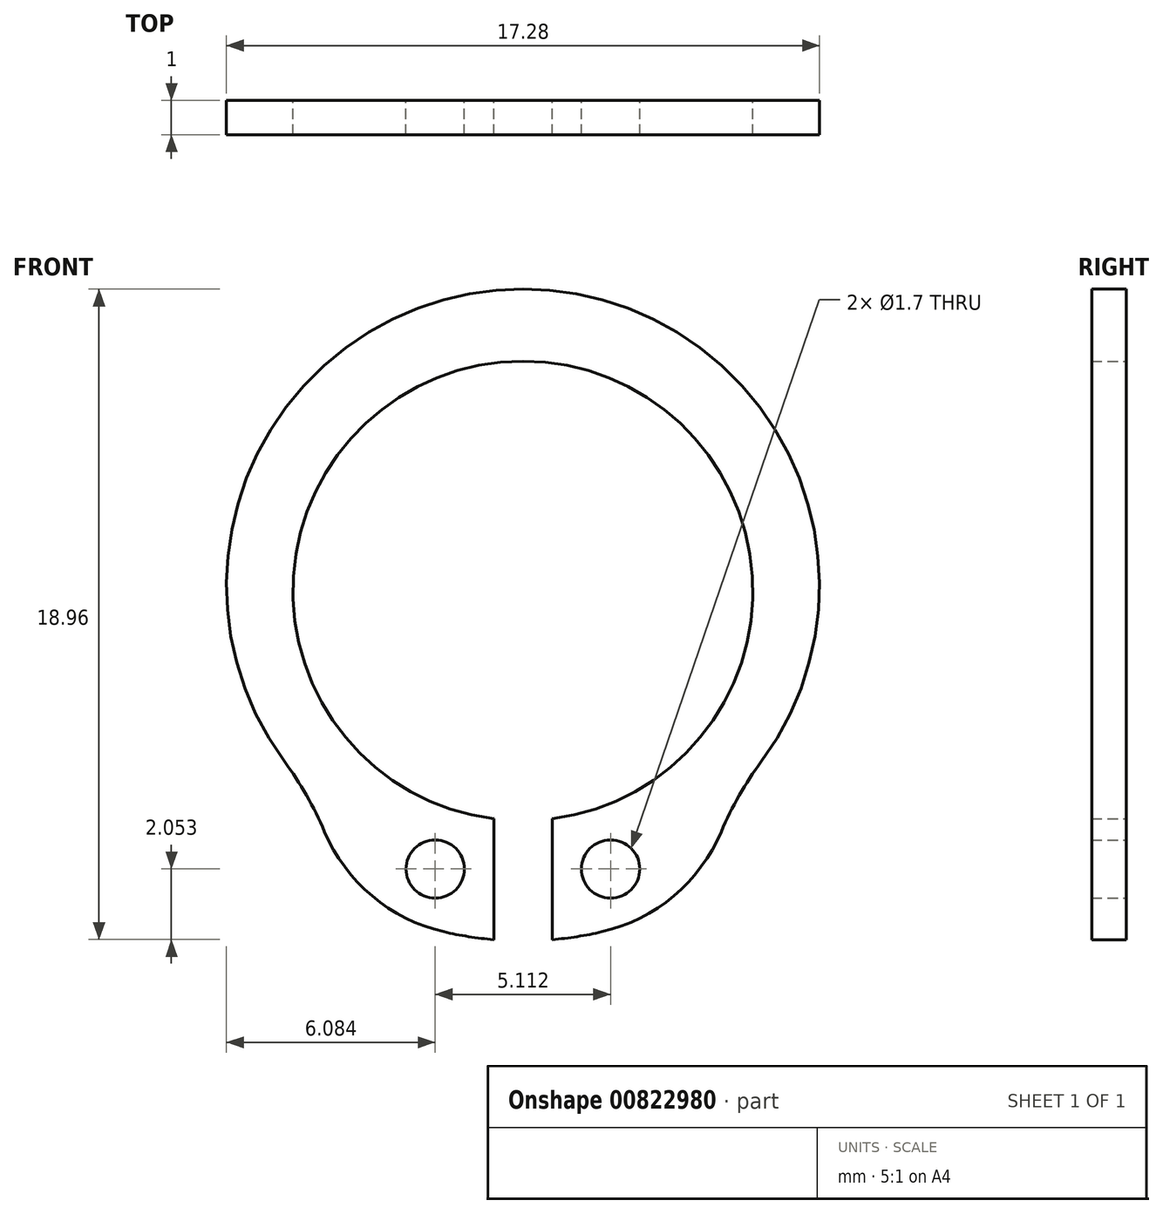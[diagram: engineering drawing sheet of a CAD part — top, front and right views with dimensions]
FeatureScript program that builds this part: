
annotation { "Feature Type Name" : "Feature", "Feature Type Description" : "" }
export const myFeature = defineFeature(function(context is Context, id is Id, definition is map)
    precondition{}
    {
        {
            var Q0;
            Q0=qCreatedBy(makeId("Front.planeOp"),FACE);
            var sketch = newSketch(context, id + "F0", { "sketchPlane" : qUnion([Q0])});
            skArc(sketch, "E0", {"start": v(0.85, -6.65) * mm, "mid": v(0, 6.7) * mm, "end": v(-0.85, -6.65) * mm});
            skCircle(sketch, "E1.0", {"center": v(0, 0) * mm, "radius": 8.8 * mm, "construction": true});
            skArc(sketch, "E2.0", {"start": v(0.85, -10.16) * mm, "mid": v(3.12, -9.71) * mm, "end": v(5.22, -8.76) * mm});
            skLineSegment(sketch, "E3", {"start": v(0, -10.2) * mm, "end": v(0, 10.2) * mm, "construction": true});
            skLineSegment(sketch, "E4.0", {"start": v(0.85, -16.35) * mm, "end": v(0.85, -6.65) * mm});
            skLineSegment(sketch, "E5.0", {"start": v(-0.85, -16.35) * mm, "end": v(-0.85, -6.65) * mm});
            skCircle(sketch, "E6", {"center": v(2.56, -8.1) * mm, "radius": 0.85 * mm});
            skLineSegment(sketch, "E7", {"start": v(2.56, -8.1) * mm, "end": v(0, 0) * mm, "construction": true});
            skCircle(sketch, "E8", {"center": v(0, 0) * mm, "radius": 8.5 * mm, "construction": true});
            skCircle(sketch, "E9.MirrorC", {"center": v(-2.56, -8.1) * mm, "radius": 0.85 * mm});
            skLineSegment(sketch, "E10", {"start": v(5.22, -8.76) * mm, "end": v(4.5, -7.21) * mm});
            skLineSegment(sketch, "E11.trimOffspring", {"start": v(-4.5, -7.21) * mm, "end": v(-5.22, -8.76) * mm});
            skPoint(sketch, "E12", {"position": v(0, 8.8) * mm});
            skArc(sketch, "E13", {"start": v(4.5, -7.21) * mm, "mid": v(0, 8.8) * mm, "end": v(-4.5, -7.21) * mm});
            skArc(sketch, "E14.trimOffspring", {"start": v(-5.22, -8.76) * mm, "mid": v(-3.12, -9.71) * mm, "end": v(-0.85, -10.16) * mm});
            skArc(sketch, "E15.trimOffspring", {"start": v(0.07, 10.2) * mm, "mid": v(-0.04, 10.2) * mm, "end": v(-0.16, 10.2) * mm});
            skSolve(sketch);
        }
        {
            var Q0;
            Q0=qSketchRegion(id+"F0",true);
            extrude(context, id + "F1", {"entities" : qUnion([Q0]), "depth" : 1 * mm, "offsetDistance" : 25 * mm});
        }
        {
            var Q0;
            Q0=makeQuery(id+"F1.opExtrude","SWEPT_EDGE",EDGE,{"disambiguationData":[OSD([sQuery(id+"F0.wireOp",EDGE,"E11.trimOffspring"),sQuery(id+"F0.wireOp",EDGE,"E13")])]});
            var Q1;
            Q1=makeQuery(id+"F1.opExtrude","SWEPT_EDGE",EDGE,{"disambiguationData":[OSD([sQuery(id+"F0.wireOp",EDGE,"E10"),sQuery(id+"F0.wireOp",EDGE,"E13")])]});
            fillet(context, id + "F2", {"entities" : qUnion([Q0, Q1]), "radius" : 10 * mm, "tangentPropagation" : true, "allowEdgeOverflow" : false});
        }
        {
            var Q0;
            Q0=makeQuery(id+"F2.opFillet","BLEND_EDGE",EDGE,{"blendedFrom":[makeQuery(id+"F1.opExtrude","SWEPT_EDGE",EDGE,{"disambiguationData":[OSD([sQuery(id+"F0.wireOp",EDGE,"E11.trimOffspring"),sQuery(id+"F0.wireOp",EDGE,"E13")])]}),makeQuery(id+"F1.opExtrude","SWEPT_FACE",FACE,{"disambiguationData":[OSD([sQuery(id+"F0.wireOp",EDGE,"E14.trimOffspring")])]})],"blendedInto":[makeQuery(id+"F1.opExtrude","SWEPT_FACE",FACE,{"disambiguationData":[OSD([sQuery(id+"F0.wireOp",EDGE,"E14.trimOffspring")])]})]});
            var Q1;
            Q1=makeQuery(id+"F2.opFillet","BLEND_EDGE",EDGE,{"blendedFrom":[makeQuery(id+"F1.opExtrude","SWEPT_EDGE",EDGE,{"disambiguationData":[OSD([sQuery(id+"F0.wireOp",EDGE,"E10"),sQuery(id+"F0.wireOp",EDGE,"E13")])]}),makeQuery(id+"F1.opExtrude","SWEPT_FACE",FACE,{"disambiguationData":[OSD([sQuery(id+"F0.wireOp",EDGE,"E2.0")])]})],"blendedInto":[makeQuery(id+"F1.opExtrude","SWEPT_FACE",FACE,{"disambiguationData":[OSD([sQuery(id+"F0.wireOp",EDGE,"E2.0")])]})]});
            fillet(context, id + "F3", {"entities" : qUnion([Q0, Q1]), "radius" : 5 * mm, "tangentPropagation" : true, "allowEdgeOverflow" : false});
        }
    });
